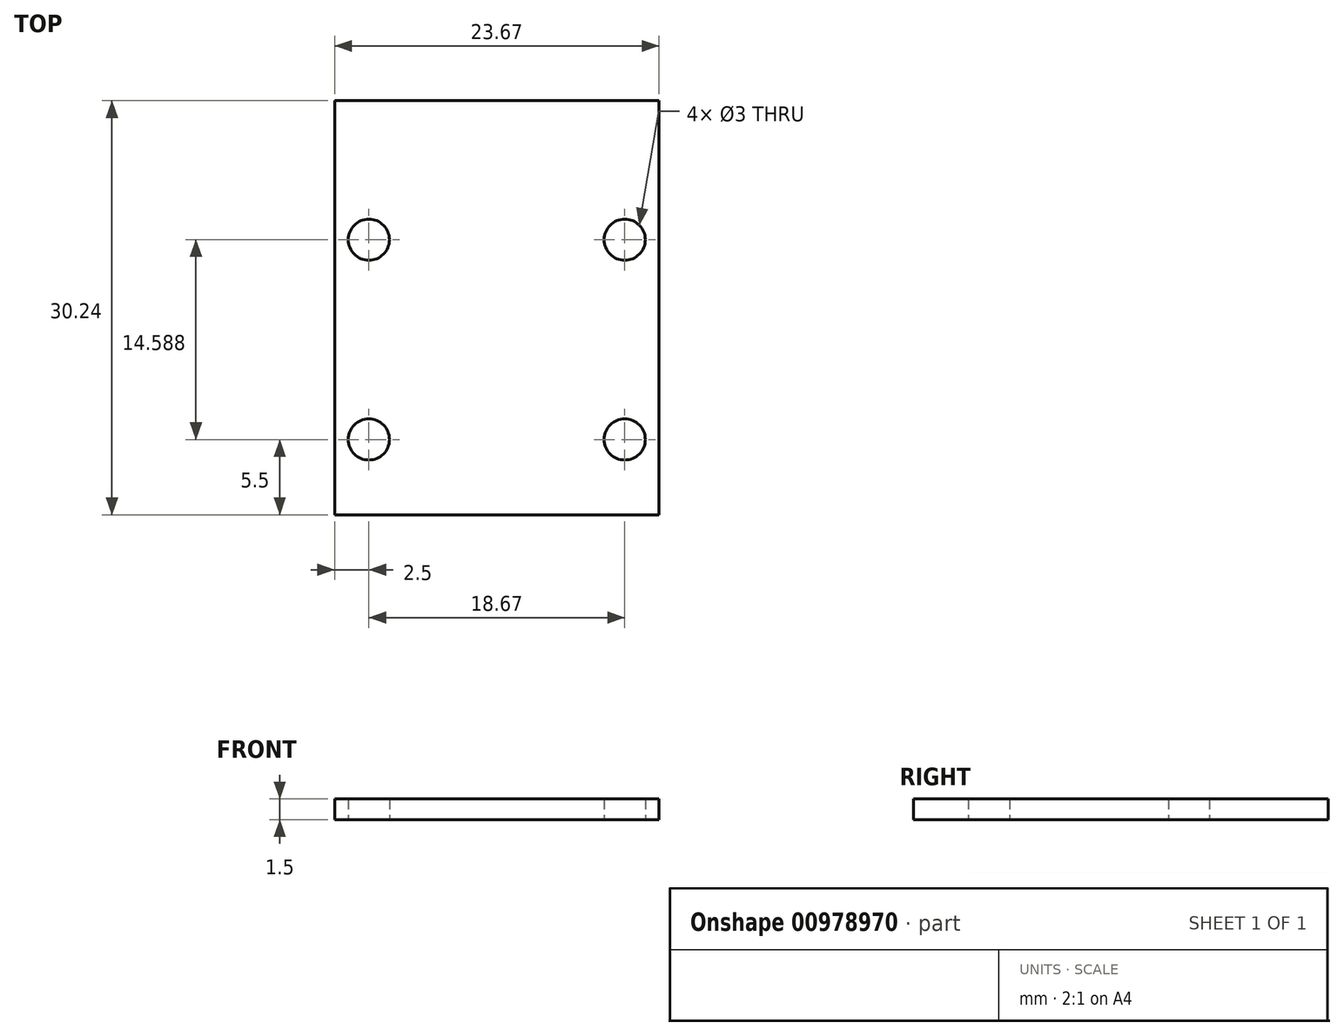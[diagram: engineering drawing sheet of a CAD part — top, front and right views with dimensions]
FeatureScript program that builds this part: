
annotation { "Feature Type Name" : "Feature", "Feature Type Description" : "" }
export const myFeature = defineFeature(function(context is Context, id is Id, definition is map)
    precondition{}
    {
        {
            var Q0;
            Q0=qCreatedBy(makeId("Top.planeOp"),FACE);
            var sketch = newSketch(context, id + "F0", { "sketchPlane" : qUnion([Q0])});
            skLineSegment(sketch, "E0.bottom", {"start": v(-23.67, 39.6) * mm, "end": v(0, 39.6) * mm});
            skLineSegment(sketch, "E0.top", {"start": v(-23.67, 9.36) * mm, "end": v(0, 9.36) * mm});
            skLineSegment(sketch, "E0.left", {"start": v(-23.67, 39.6) * mm, "end": v(-23.67, 9.36) * mm});
            skLineSegment(sketch, "E0.right", {"start": v(0, 39.6) * mm, "end": v(0, 9.36) * mm});
            skCircle(sketch, "E1", {"center": v(-21.17, 29.45) * mm, "radius": 1.5 * mm});
            skCircle(sketch, "E2", {"center": v(-2.5, 29.45) * mm, "radius": 1.5 * mm});
            skLineSegment(sketch, "E3", {"start": v(-23.67, 9.36) * mm, "end": v(-23.67, 13.36) * mm});
            skLineSegment(sketch, "E4", {"start": v(-23.67, 13.36) * mm, "end": v(-23.67, 14.86) * mm});
            skCircle(sketch, "E5", {"center": v(-21.17, 14.86) * mm, "radius": 1.5 * mm});
            skCircle(sketch, "E6", {"center": v(-2.5, 14.86) * mm, "radius": 1.5 * mm});
            skSolve(sketch);
        }
        {
            var Q0;
            Q0=qSketchRegion(id+"F0",true);
            var Q1;
            Q1=makeQuery(id+"F0.imprint","IMPRINT",FACE,{"disambiguationData":[TD([[makeQuery(id+"F0.imprint","IMPRINT",EDGE,{"derivedFrom":sQuery(id+"F0.wireOp",EDGE,"E0.bottom")}),-1.0]])]});
            extrude(context, id + "F1", {"entities" : qUnion([Q0, Q1]), "depth" : 1.5 * mm, "offsetDistance" : 25 * mm});
        }
    });
